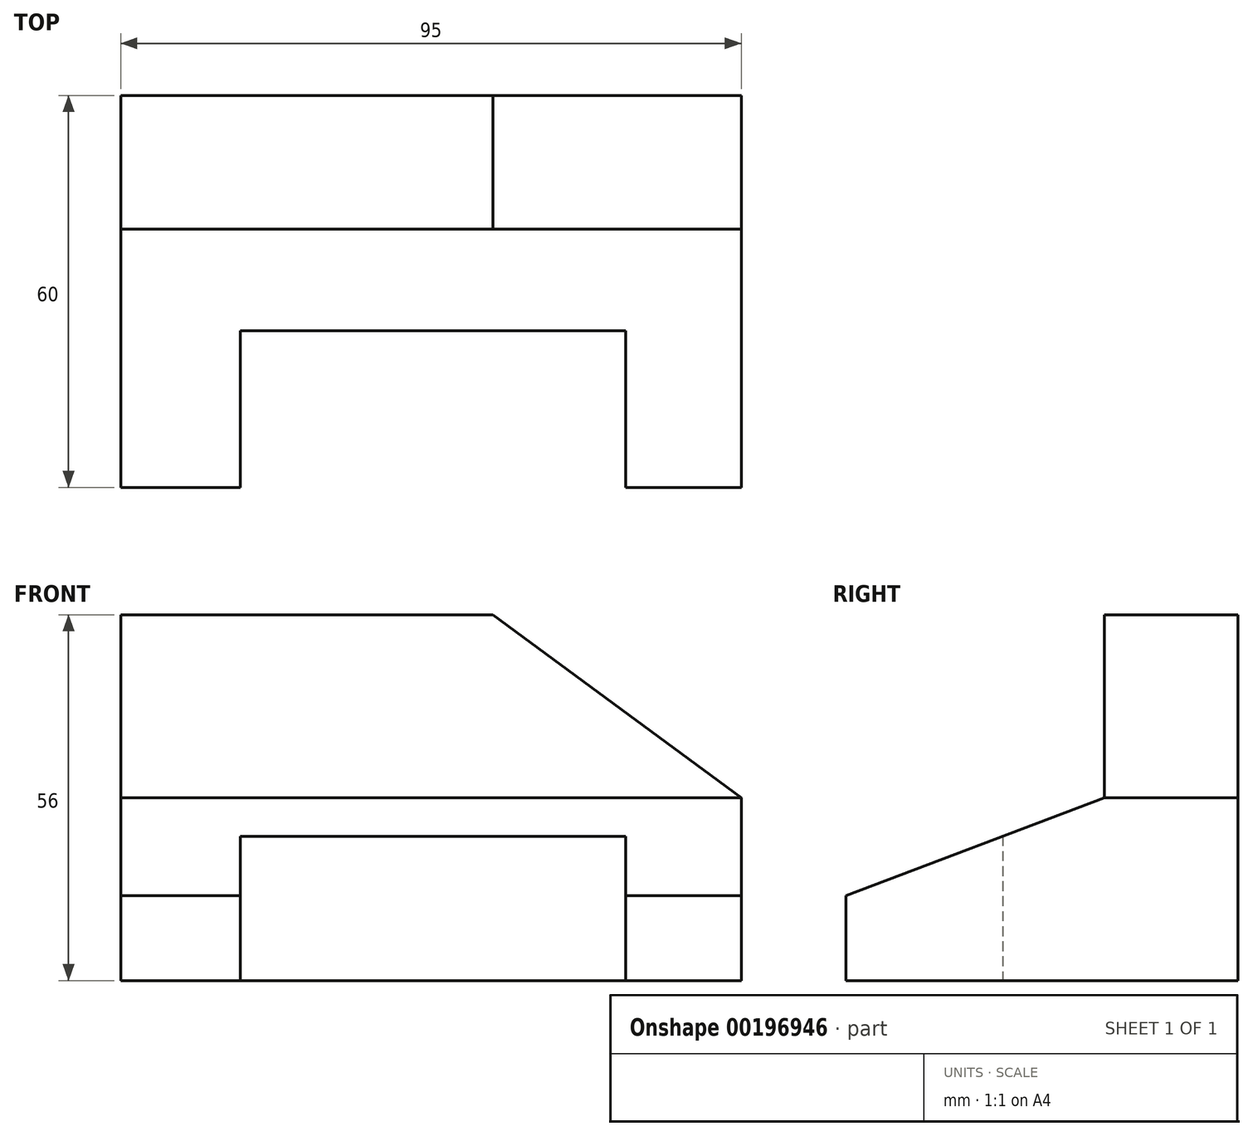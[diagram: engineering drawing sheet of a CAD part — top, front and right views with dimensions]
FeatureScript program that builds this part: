
annotation { "Feature Type Name" : "Feature", "Feature Type Description" : "" }
export const myFeature = defineFeature(function(context is Context, id is Id, definition is map)
    precondition{}
    {
        {
            var Q0;
            Q0=qCreatedBy(makeId("Right.planeOp"),FACE);
            var sketch = newSketch(context, id + "F0", { "sketchPlane" : qUnion([Q0])});
            skLineSegment(sketch, "E0", {"start": v(-54.52, -33.17) * mm, "end": v(5.48, -33.17) * mm});
            skLineSegment(sketch, "E1", {"start": v(5.48, -33.17) * mm, "end": v(5.48, -5.17) * mm});
            skLineSegment(sketch, "E2", {"start": v(5.48, -5.17) * mm, "end": v(-14.97, -5.17) * mm});
            skLineSegment(sketch, "E3", {"start": v(-14.97, -5.17) * mm, "end": v(-54.52, -20.17) * mm});
            skLineSegment(sketch, "E4", {"start": v(-54.52, -20.17) * mm, "end": v(-54.52, -33.17) * mm});
            skLineSegment(sketch, "E5", {"start": v(5.48, -5.17) * mm, "end": v(5.48, 22.83) * mm});
            skLineSegment(sketch, "E6", {"start": v(5.48, 22.83) * mm, "end": v(-14.97, 22.83) * mm});
            skLineSegment(sketch, "E7", {"start": v(-14.97, 22.83) * mm, "end": v(-14.97, -5.17) * mm});
            skSolve(sketch);
        }
        {
            var Q0;
            Q0=makeQuery(id+"F0.imprint","IMPRINT",FACE,{"disambiguationData":[TD([[makeQuery(id+"F0.imprint","IMPRINT",EDGE,{"derivedFrom":sQuery(id+"F0.wireOp",EDGE,"E2")}),-1.0]])]});
            var Q1;
            Q1=makeQuery(id+"F0.imprint","IMPRINT",FACE,{"disambiguationData":[TD([[makeQuery(id+"F0.imprint","IMPRINT",EDGE,{"derivedFrom":sQuery(id+"F0.wireOp",EDGE,"E0")}),1.0]])]});
            extrude(context, id + "F1", {"entities" : qUnion([Q0, Q1]), "oppositeDirection" : true, "depth" : 95 * mm});
        }
        {
            var Q0;
            Q0=makeQuery(id+"F1.opExtrude","SWEPT_FACE",FACE,{"disambiguationData":[OSD([sQuery(id+"F0.wireOp",EDGE,"E7")])]});
            var sketch = newSketch(context, id + "F2", { "sketchPlane" : qUnion([Q0])});
            skLineSegment(sketch, "E8", {"start": v(-38, 22.83) * mm, "end": v(0, -5.17) * mm});
            skSolve(sketch);
        }
        {
            var Q0;
            {var subQ0=sQuery(id+"F2.wireOp",EDGE,"E8");Q0=makeQuery(id+"F2.imprint","IMPRINT",FACE,{"disambiguationData":[TD([[makeQuery(id+"F2.imprint","IMPRINT",EDGE,{"derivedFrom":subQ0}),1.0]])]});}
            extrude(context, id + "F3", {"entities" : qUnion([Q0]), "operationType" : NewBodyOperationType.REMOVE, "oppositeDirection" : true, "depth" : 25 * mm});
        }
        {
            var Q0;
            Q0=makeQuery(id+"F1.opExtrude","SWEPT_FACE",FACE,{"disambiguationData":[OSD([sQuery(id+"F0.wireOp",EDGE,"E0")])]});
            var sketch = newSketch(context, id + "F4", { "sketchPlane" : qUnion([Q0])});
            skLineSegment(sketch, "E9", {"start": v(-76.7, 54.52) * mm, "end": v(-76.7, 30.52) * mm});
            skLineSegment(sketch, "E10", {"start": v(-76.7, 30.52) * mm, "end": v(-17.7, 30.52) * mm});
            skLineSegment(sketch, "E11", {"start": v(-17.7, 30.52) * mm, "end": v(-17.7, 54.52) * mm});
            skLineSegment(sketch, "E12", {"start": v(-76.7, 54.52) * mm, "end": v(-17.7, 54.52) * mm});
            skSolve(sketch);
        }
        {
            var Q0;
            Q0=makeQuery(id+"F4.imprint","IMPRINT",FACE,{"disambiguationData":[TD([[makeQuery(id+"F4.imprint","IMPRINT",EDGE,{"derivedFrom":sQuery(id+"F4.wireOp",EDGE,"E9")}),1.0]])]});
            extrude(context, id + "F5", {"entities" : qUnion([Q0]), "operationType" : NewBodyOperationType.REMOVE, "oppositeDirection" : true, "depth" : 25 * mm});
        }
    });
